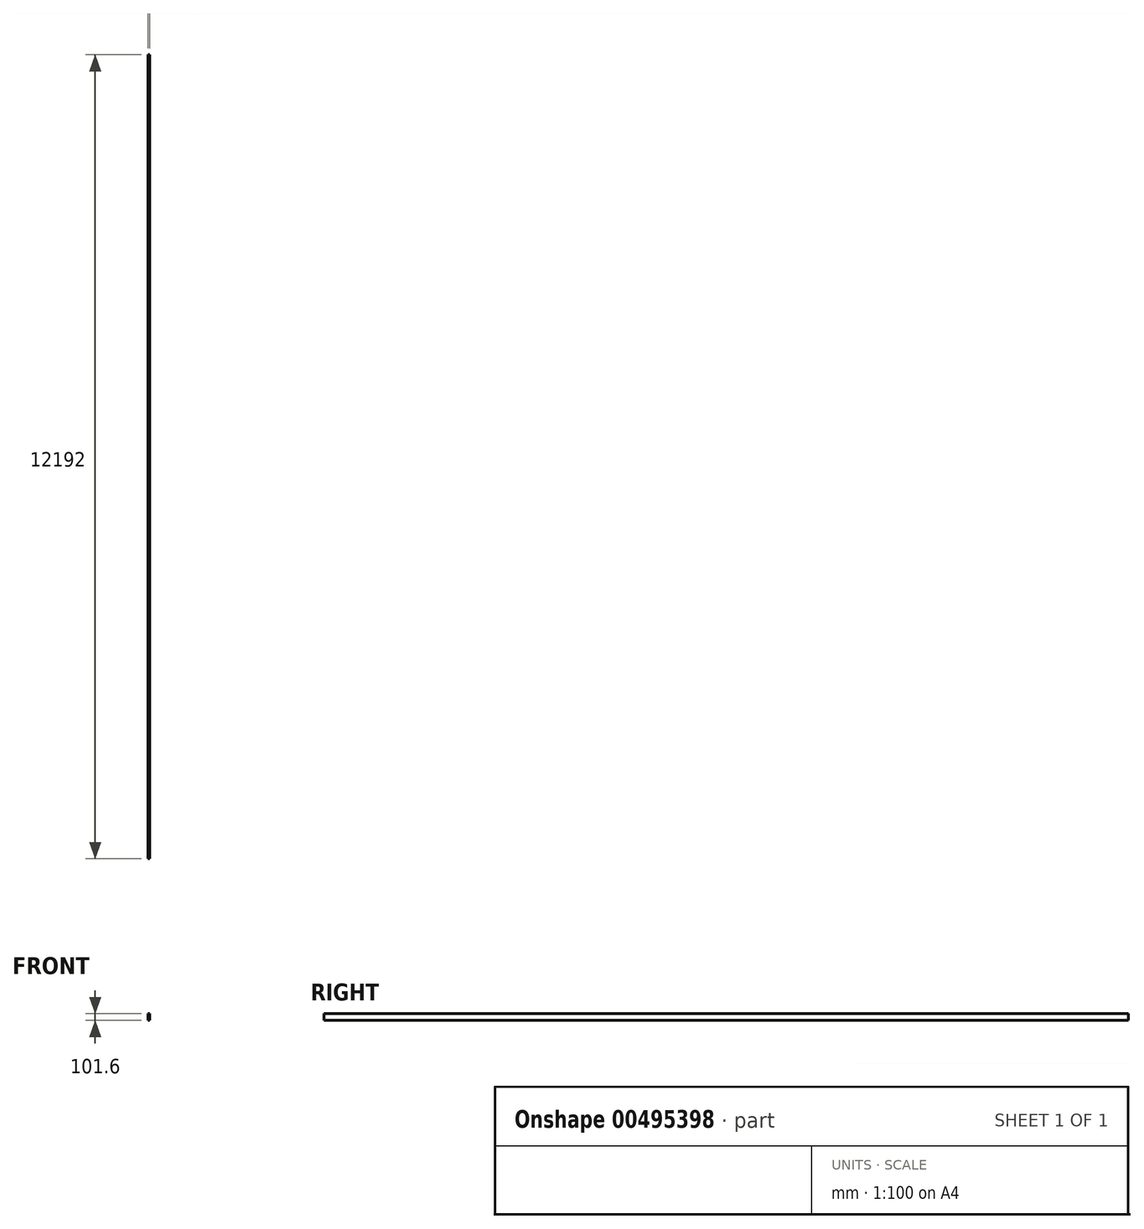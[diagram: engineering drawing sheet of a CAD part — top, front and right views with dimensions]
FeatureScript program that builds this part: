
annotation { "Feature Type Name" : "Feature", "Feature Type Description" : "" }
export const myFeature = defineFeature(function(context is Context, id is Id, definition is map)
    precondition{}
    {
        {
            var Q0;
            Q0=qCreatedBy(makeId("Front.planeOp"),FACE);
            var sketch = newSketch(context, id + "F0", { "sketchPlane" : qUnion([Q0])});
            skLineSegment(sketch, "E0.bottom", {"start": v(0, 0) * mm, "end": v(25.4, 0) * mm});
            skLineSegment(sketch, "E0.top", {"start": v(0, 101.6) * mm, "end": v(25.4, 101.6) * mm});
            skLineSegment(sketch, "E0.left", {"start": v(0, 0) * mm, "end": v(0, 101.6) * mm});
            skLineSegment(sketch, "E0.right", {"start": v(25.4, 0) * mm, "end": v(25.4, 101.6) * mm});
            skSolve(sketch);
        }
        {
            var Q0;
            Q0 = qSketchRegion(id + "F0", true);
            extrude(context, id + "F1", {"entities" : qUnion([Q0]), "depth" : 12192 * mm, "offsetDistance" : 25.4 * mm});
        }
    });
